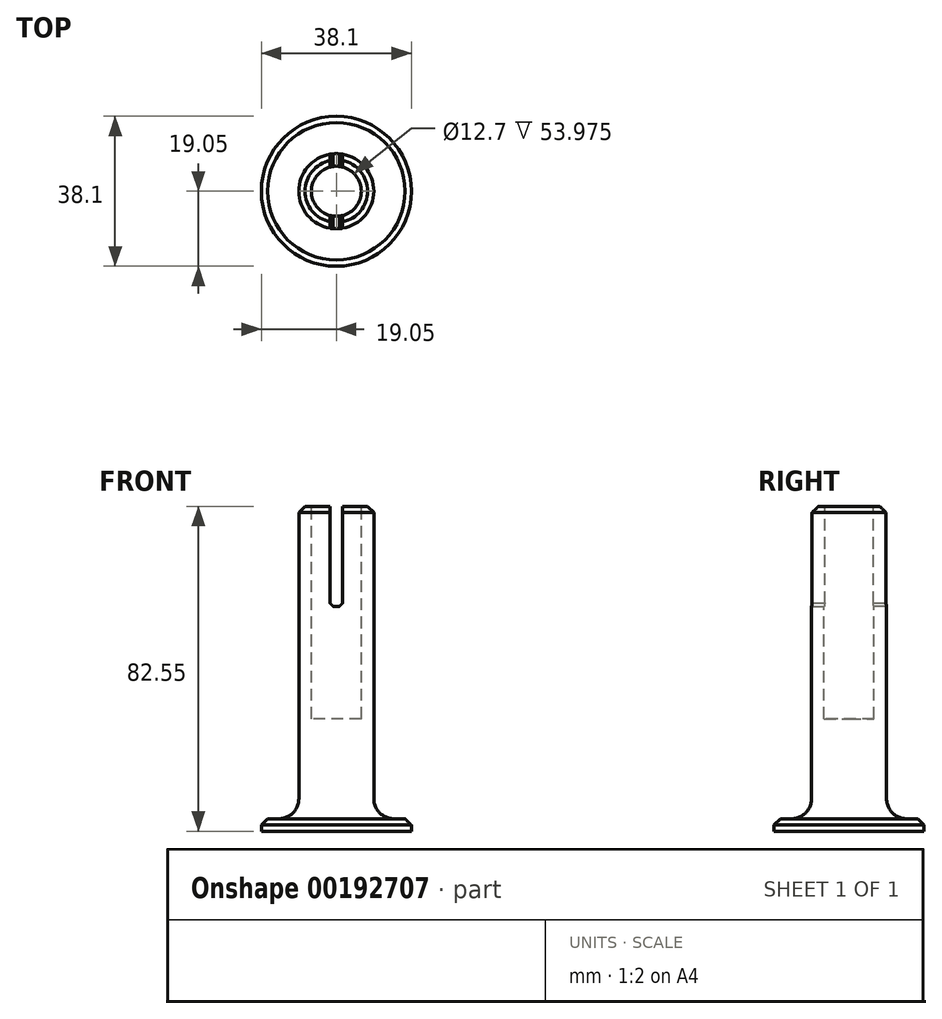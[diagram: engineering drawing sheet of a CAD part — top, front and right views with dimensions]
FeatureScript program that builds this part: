
annotation { "Feature Type Name" : "Feature", "Feature Type Description" : "" }
export const myFeature = defineFeature(function(context is Context, id is Id, definition is map)
    precondition{}
    {
        {
            var Q0;
            Q0=qCreatedBy(makeId("Top.planeOp"),FACE);
            var sketch = newSketch(context, id + "F0", { "sketchPlane" : qUnion([Q0])});
            skCircle(sketch, "E0", {"center": v(0, 0) * mm, "radius": 9.53 * mm});
            skSolve(sketch);
        }
        {
            var Q0;
            Q0=makeQuery(id+"F0.imprint","IMPRINT",FACE,{"disambiguationData":[TD([[makeQuery(id+"F0.imprint","IMPRINT",EDGE,{"derivedFrom":sQuery(id+"F0.wireOp",EDGE,"E0")}),1.0]])]});
            extrude(context, id + "F1", {"entities" : qUnion([Q0]), "depth" : 82.55 * mm});
        }
        {
            var Q0;
            Q0=qCreatedBy(makeId("Top.planeOp"),FACE);
            var sketch = newSketch(context, id + "F2", { "sketchPlane" : qUnion([Q0])});
            skCircle(sketch, "E1", {"center": v(0, 0) * mm, "radius": 19.05 * mm});
            skSolve(sketch);
        }
        {
            var Q0;
            Q0 = qSketchRegion(id + "F2", true);
            extrude(context, id + "F3", {"entities" : qUnion([Q0]), "operationType" : NewBodyOperationType.ADD, "depth" : 3.17 * mm});
        }
        {
            var Q0;
            Q0=makeQuery(id+"F1.opExtrude","CAP_FACE",FACE,{"disambiguationData":[OSD([sQuery(id+"F0.wireOp",EDGE,"E0")])],"isStart":false});
            var sketch = newSketch(context, id + "F4", { "sketchPlane" : qUnion([Q0])});
            skCircle(sketch, "E2", {"center": v(0, 0) * mm, "radius": 6.35 * mm});
            skSolve(sketch);
        }
        {
            var Q0;
            Q0 = qSketchRegion(id + "F4", true);
            extrude(context, id + "F5", {"entities" : qUnion([Q0]), "operationType" : NewBodyOperationType.REMOVE, "oppositeDirection" : true, "depth" : 53.97 * mm});
        }
        {
            var Q0;
            Q0=makeQuery(id+"F3.boolean.opBoolean","INTERSECT",EDGE,{"derivedFrom":[makeQuery(id+"F1.opExtrude","SWEPT_FACE",FACE,{"disambiguationData":[OSD([sQuery(id+"F0.wireOp",EDGE,"E0")])]}),makeQuery(id+"F3.opExtrude","CAP_FACE",FACE,{"disambiguationData":[OSD([sQuery(id+"F2.wireOp",EDGE,"E1")])],"isStart":false})]});
            fillet(context, id + "F6", {"entities" : qUnion([Q0]), "radius" : 5.08 * mm, "tangentPropagation" : true, "allowEdgeOverflow" : false});
        }
        {
            var Q0;
            Q0=makeQuery(id+"F1.opExtrude","CAP_EDGE",EDGE,{"disambiguationData":[OSD([sQuery(id+"F0.wireOp",EDGE,"E0")])],"isStart":false});
            var Q1;
            Q1=makeQuery(id+"F3.opExtrude","CAP_EDGE",EDGE,{"disambiguationData":[OSD([sQuery(id+"F2.wireOp",EDGE,"E1")])],"isStart":false});
            chamfer(context, id + "F7", {"entities" : qUnion([Q0, Q1]), "width" : 1.59 * mm, "tangentPropagation" : true});
        }
        {
            var Q0;
            Q0=makeQuery(id+"F1.opExtrude","CAP_FACE",FACE,{"disambiguationData":[OSD([sQuery(id+"F0.wireOp",EDGE,"E0")])],"isStart":false});
            var sketch = newSketch(context, id + "F8", { "sketchPlane" : qUnion([Q0])});
            skLineSegment(sketch, "E3", {"start": v(0, 0) * mm, "end": v(0, 25.4) * mm});
            skLineSegment(sketch, "E4", {"start": v(0, 25.4) * mm, "end": v(1.59, 25.4) * mm});
            skLineSegment(sketch, "E5", {"start": v(1.59, 25.4) * mm, "end": v(1.59, 0) * mm});
            skLineSegment(sketch, "E6", {"start": v(1.59, 0) * mm, "end": v(0, 0) * mm});
            skLineSegment(sketch, "E7.MirrorCS", {"start": v(0, 25.4) * mm, "end": v(-1.59, 25.4) * mm});
            skLineSegment(sketch, "E8.MirrorCS", {"start": v(-1.59, 25.4) * mm, "end": v(-1.59, 0) * mm});
            skLineSegment(sketch, "E9.MirrorCS", {"start": v(0, -25.4) * mm, "end": v(1.59, -25.4) * mm});
            skLineSegment(sketch, "E10.MirrorCS", {"start": v(0, -25.4) * mm, "end": v(-1.59, -25.4) * mm});
            skLineSegment(sketch, "E11.MirrorCS", {"start": v(-1.59, -25.4) * mm, "end": v(-1.59, 0) * mm});
            skLineSegment(sketch, "E12.MirrorCS", {"start": v(1.59, -25.4) * mm, "end": v(1.59, 0) * mm});
            skSolve(sketch);
        }
        {
            var Q0;
            Q0 = qSketchRegion(id + "F8", true);
            extrude(context, id + "F9", {"entities" : qUnion([Q0]), "operationType" : NewBodyOperationType.REMOVE, "oppositeDirection" : true, "depth" : 25.4 * mm});
        }
        {
            var Q0;
            Q0=makeQuery(id+"F9.boolean.opBoolean","COPY",EDGE,{"disambiguationData":[OD(1.0)],"derivedFrom":makeQuery(id+"F9.opExtrude","CAP_EDGE",EDGE,{"disambiguationData":[OSD([sQuery(id+"F8.wireOp",EDGE,"E5"),sQuery(id+"F8.wireOp",EDGE,"E12.MirrorCS")])],"isStart":false})});
            var Q1;
            Q1=makeQuery(id+"F9.boolean.opBoolean","COPY",EDGE,{"disambiguationData":[OD(0.0)],"derivedFrom":makeQuery(id+"F9.opExtrude","CAP_EDGE",EDGE,{"disambiguationData":[OSD([sQuery(id+"F8.wireOp",EDGE,"E5"),sQuery(id+"F8.wireOp",EDGE,"E12.MirrorCS")])],"isStart":false})});
            var Q2;
            Q2=makeQuery(id+"F9.boolean.opBoolean","COPY",EDGE,{"disambiguationData":[OD(1.0)],"derivedFrom":makeQuery(id+"F9.opExtrude","CAP_EDGE",EDGE,{"disambiguationData":[OSD([sQuery(id+"F8.wireOp",EDGE,"E8.MirrorCS"),sQuery(id+"F8.wireOp",EDGE,"E11.MirrorCS")])],"isStart":false})});
            var Q3;
            Q3=makeQuery(id+"F9.boolean.opBoolean","COPY",EDGE,{"disambiguationData":[OD(0.0)],"derivedFrom":makeQuery(id+"F9.opExtrude","CAP_EDGE",EDGE,{"disambiguationData":[OSD([sQuery(id+"F8.wireOp",EDGE,"E8.MirrorCS"),sQuery(id+"F8.wireOp",EDGE,"E11.MirrorCS")])],"isStart":false})});
            chamfer(context, id + "F10", {"entities" : qUnion([Q0, Q1, Q2, Q3]), "width" : 0.8 * mm, "tangentPropagation" : true});
        }
    });
